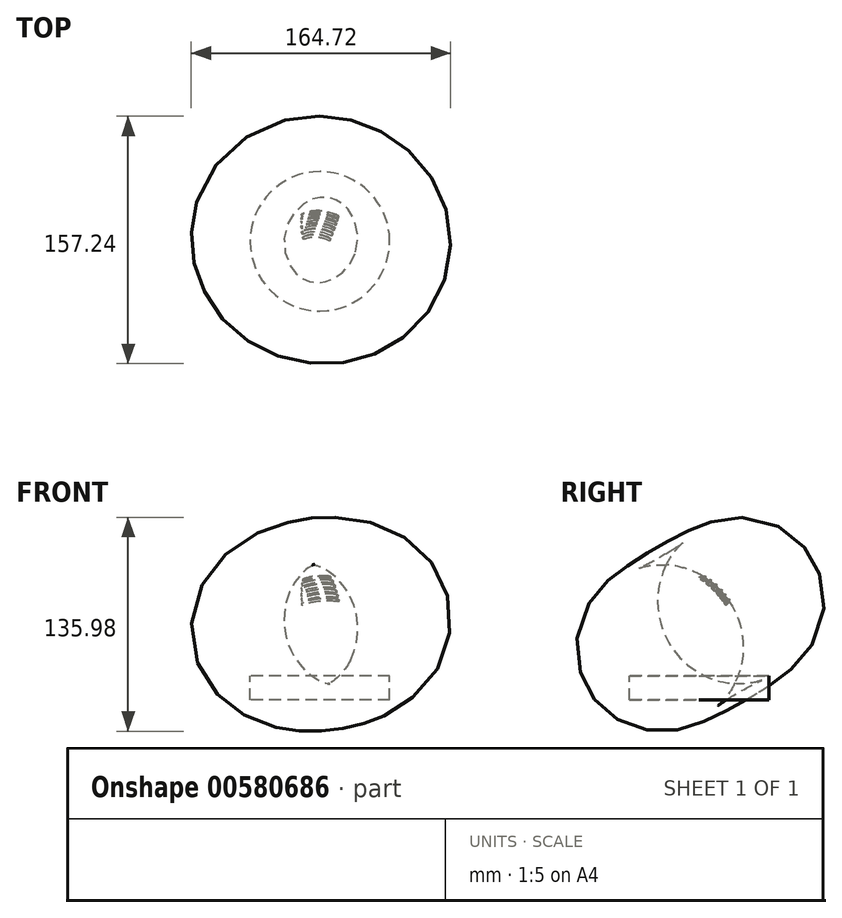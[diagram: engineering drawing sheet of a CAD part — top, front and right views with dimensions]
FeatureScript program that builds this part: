
annotation { "Feature Type Name" : "Feature", "Feature Type Description" : "" }
export const myFeature = defineFeature(function(context is Context, id is Id, definition is map)
    precondition{}
    {
        {
            var Q0;
            Q0=qCreatedBy(makeId("Front.planeOp"),FACE);
            var sketch = newSketch(context, id + "F0", { "sketchPlane" : qUnion([Q0])});
            skLineSegment(sketch, "E0", {"start": v(-43.8, 0) * mm, "end": v(43.8, 0) * mm});
            skArc(sketch, "E1", {"start": v(43.8, 0) * mm, "mid": v(0, 23.24) * mm, "end": v(-43.8, 0) * mm});
            skSolve(sketch);
        }
        {
            var Q0;
            Q0=makeQuery(id+"F0.imprint","IMPRINT",FACE,{"disambiguationData":[TD([[makeQuery(id+"F0.imprint","IMPRINT",EDGE,{"derivedFrom":sQuery(id+"F0.wireOp",EDGE,"E0")}),1.0]])]});
            var Q1;
            Q1=sQuery(id+"F0.wireOp",EDGE,"E0");
            revolve(context, id + "F1", {"entities" : qUnion([Q0]), "axis" : qUnion([Q1]), "revolveType" : RevolveType.FULL});
        }
        {
            var Q0;
            Q0=qCreatedBy(makeId("Front.planeOp"),FACE);
            var sketch = newSketch(context, id + "F2", { "sketchPlane" : qUnion([Q0])});
            skArc(sketch, "E2.0", {"start": v(43.8, 0) * mm, "mid": v(0, 23.24) * mm, "end": v(-43.8, 0) * mm});
            skLineSegment(sketch, "E3", {"start": v(-25.6, 16.62) * mm, "end": v(-25.13, 18.12) * mm});
            skLineSegment(sketch, "E4", {"start": v(-25.13, 18.12) * mm, "end": v(-23.65, 17.65) * mm});
            skLineSegment(sketch, "E5", {"start": v(-23.65, 17.65) * mm, "end": v(-21.86, 18.5) * mm});
            skLineSegment(sketch, "E6", {"start": v(-21.86, 18.5) * mm, "end": v(-21.12, 20.01) * mm});
            skLineSegment(sketch, "E7", {"start": v(-21.12, 20.01) * mm, "end": v(-19.33, 19.58) * mm});
            skLineSegment(sketch, "E8", {"start": v(-19.33, 19.58) * mm, "end": v(-17.47, 20.27) * mm});
            skLineSegment(sketch, "E9", {"start": v(-17.47, 20.27) * mm, "end": v(-17, 21.56) * mm});
            skLineSegment(sketch, "E10", {"start": v(-17, 21.56) * mm, "end": v(-14.88, 21.1) * mm});
            skLineSegment(sketch, "E11", {"start": v(-14.88, 21.1) * mm, "end": v(-12.92, 21.63) * mm});
            skLineSegment(sketch, "E12", {"start": v(-12.92, 21.63) * mm, "end": v(-12.37, 22.87) * mm});
            skLineSegment(sketch, "E13", {"start": v(-12.37, 22.87) * mm, "end": v(-10.72, 22.14) * mm});
            skLineSegment(sketch, "E14", {"start": v(-10.72, 22.14) * mm, "end": v(-9.29, 22.42) * mm});
            skLineSegment(sketch, "E15", {"start": v(-9.29, 22.42) * mm, "end": v(-8.53, 23.39) * mm});
            skLineSegment(sketch, "E16", {"start": v(-8.53, 23.39) * mm, "end": v(-6.8, 22.8) * mm});
            skLineSegment(sketch, "E17", {"start": v(-6.8, 22.8) * mm, "end": v(-5.66, 22.93) * mm});
            skLineSegment(sketch, "E18", {"start": v(-5.66, 22.93) * mm, "end": v(-4.64, 24.08) * mm});
            skLineSegment(sketch, "E19", {"start": v(-4.64, 24.08) * mm, "end": v(-3.57, 23.12) * mm});
            skSolve(sketch);
        }
        {
            var Q0;
            {var subQ0=sQuery(id+"F2.wireOp",EDGE,"E3");Q0=makeQuery(id+"F2.imprint","IMPRINT",FACE,{"disambiguationData":[TD([[makeQuery(id+"F2.imprint","IMPRINT",EDGE,{"derivedFrom":subQ0}),-1.0]])]});}
            var Q1;
            {var subQ0=sQuery(id+"F2.wireOp",EDGE,"E6");Q1=makeQuery(id+"F2.imprint","IMPRINT",FACE,{"disambiguationData":[TD([[makeQuery(id+"F2.imprint","IMPRINT",EDGE,{"derivedFrom":subQ0}),-1.0]])]});}
            var Q2;
            {var subQ0=sQuery(id+"F2.wireOp",EDGE,"E9");Q2=makeQuery(id+"F2.imprint","IMPRINT",FACE,{"disambiguationData":[TD([[makeQuery(id+"F2.imprint","IMPRINT",EDGE,{"derivedFrom":subQ0}),-1.0]])]});}
            var Q3;
            {var subQ0=sQuery(id+"F2.wireOp",EDGE,"E12");Q3=makeQuery(id+"F2.imprint","IMPRINT",FACE,{"disambiguationData":[TD([[makeQuery(id+"F2.imprint","IMPRINT",EDGE,{"derivedFrom":subQ0}),-1.0]])]});}
            var Q4;
            {var subQ0=sQuery(id+"F2.wireOp",EDGE,"E15");Q4=makeQuery(id+"F2.imprint","IMPRINT",FACE,{"disambiguationData":[TD([[makeQuery(id+"F2.imprint","IMPRINT",EDGE,{"derivedFrom":subQ0}),-1.0]])]});}
            var Q5;
            {var subQ0=sQuery(id+"F2.wireOp",EDGE,"E18");Q5=makeQuery(id+"F2.imprint","IMPRINT",FACE,{"disambiguationData":[TD([[makeQuery(id+"F2.imprint","IMPRINT",EDGE,{"derivedFrom":subQ0}),-1.0]])]});}
            var Q6;
            Q6=sQuery(id+"F0.wireOp",EDGE,"E0");
            revolve(context, id + "F3", {"operationType" : NewBodyOperationType.ADD, "entities" : qUnion([Q0, Q1, Q2, Q3, Q4, Q5]), "axis" : qUnion([Q6]), "revolveType" : RevolveType.TWO_DIRECTIONS, "angle" : 30 * degree, "angleBack" : 330 * degree});
        }
        {
            var Q0;
            Q0=makeQuery(id+"F1.opRevolve","SWEPT_BODY",BODY,{"disambiguationData":[OSD([sQuery(id+"F0.wireOp",EDGE,"E0"),sQuery(id+"F0.wireOp",EDGE,"E1")])]});
            var Q1;
            Q1=makeQuery(id+"F3.opRevolve","CAP_EDGE",EDGE,{"disambiguationData":[OSD([sQuery(id+"F2.wireOp",EDGE,"E19")])],"isStart":false});
            transform(context, id + "F4", {"entities" : qUnion([Q0]), "transformType" : TransformType.ROTATION, "transformAxis" : qUnion([Q1]), "angle" : 180 * degree, "makeCopy" : false});
        }
        {
            var Q0;
            Q0=makeQuery(id+"F1.opRevolve","SWEPT_BODY",BODY,{"disambiguationData":[OSD([sQuery(id+"F0.wireOp",EDGE,"E0"),sQuery(id+"F0.wireOp",EDGE,"E1")])]});
            var Q1;
            Q1=makeQuery(id+"F1.opRevolve","SWEPT_FACE",FACE,{"disambiguationData":[OSD([sQuery(id+"F0.wireOp",EDGE,"E1")])]});
            transform(context, id + "F5", {"entities" : qUnion([Q0]), "transformType" : TransformType.ROTATION, "transformAxis" : qUnion([Q1]), "angle" : 90 * degree, "oppositeDirection" : true, "makeCopy" : false});
        }
        {
            var Q0;
            Q0=makeQuery(id+"F1.opRevolve","SWEPT_BODY",BODY,{"disambiguationData":[OSD([sQuery(id+"F0.wireOp",EDGE,"E0"),sQuery(id+"F0.wireOp",EDGE,"E1")])]});
            var Q1;
            Q1=makeQuery(id+"F1.opRevolve","SWEPT_FACE",FACE,{"disambiguationData":[OSD([sQuery(id+"F0.wireOp",EDGE,"E1")])]});
            transform(context, id + "F6", {"entities" : qUnion([Q0]), "transformType" : TransformType.ROTATION, "transformAxis" : qUnion([Q1]), "angle" : 330 * degree, "makeCopy" : false});
        }
        {
            var Q0;
            Q0=qCreatedBy(makeId("Top.planeOp"),FACE);
            var sketch = newSketch(context, id + "F7", { "sketchPlane" : qUnion([Q0])});
            skCircle(sketch, "E20", {"center": v(-49.18, -9.42) * mm, "radius": 44.3 * mm});
            skSolve(sketch);
        }
        {
            var Q0;
            Q0=qSketchRegion(id+"F7",true);
            extrude(context, id + "F8", {"entities" : qUnion([Q0]), "oppositeDirection" : true, "depth" : 15.24 * mm, "offsetDistance" : 25.4 * mm});
        }
        {
            var Q0;
            Q0=makeQuery(id+"F8.opExtrude","SWEPT_BODY",BODY,{"disambiguationData":[OSD([sQuery(id+"F7.wireOp",EDGE,"E20")])]});
            transform(context, id + "F9", {"entities" : qUnion([Q0]), "transformType" : TransformType.TRANSLATION_3D, "dx" : 68.33 * mm, "dy" : -2.54 * mm, "dz" : -13.72 * mm, "makeCopy" : false});
        }
    });
